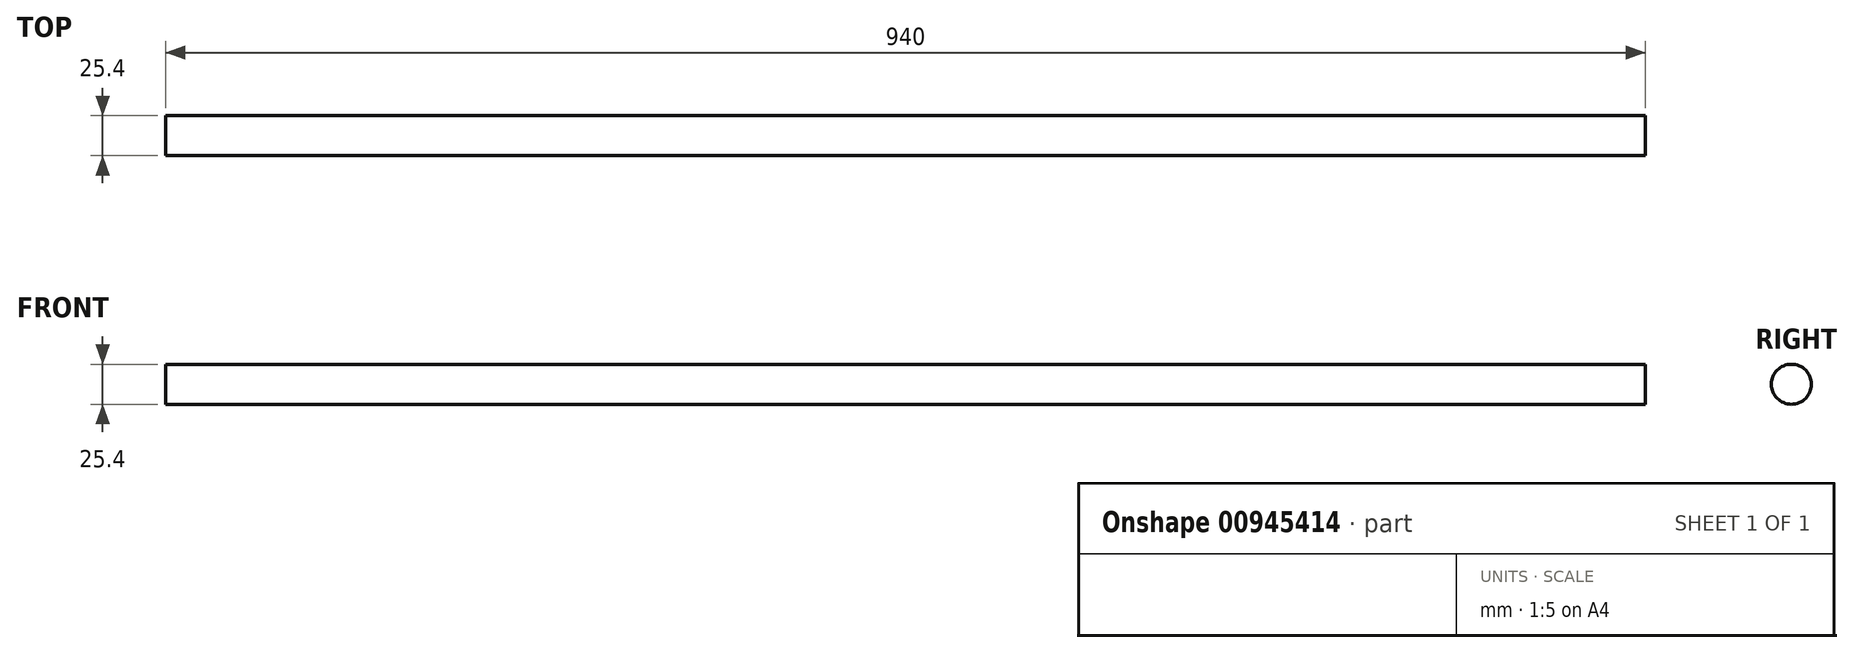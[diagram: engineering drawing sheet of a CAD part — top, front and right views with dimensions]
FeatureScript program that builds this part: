
annotation { "Feature Type Name" : "Feature", "Feature Type Description" : "" }
export const myFeature = defineFeature(function(context is Context, id is Id, definition is map)
    precondition{}
    {
        {
            var Q0;
            Q0=qCreatedBy(makeId("Right.planeOp"),FACE);
            var sketch = newSketch(context, id + "F0", { "sketchPlane" : qUnion([Q0])});
            skCircle(sketch, "E0", {"center": v(0, 0) * mm, "radius": 12.7 * mm});
            skSolve(sketch);
        }
        {
            var Q0;
            Q0=sQuery(id+"F0.wireOp",EDGE,"E0");
            extrude(context, id + "F1", {"bodyType" : ToolBodyType.SURFACE, "surfaceEntities" : qUnion([Q0]), "depth" : 940 * mm, "offsetDistance" : 25.4 * mm});
        }
    });
